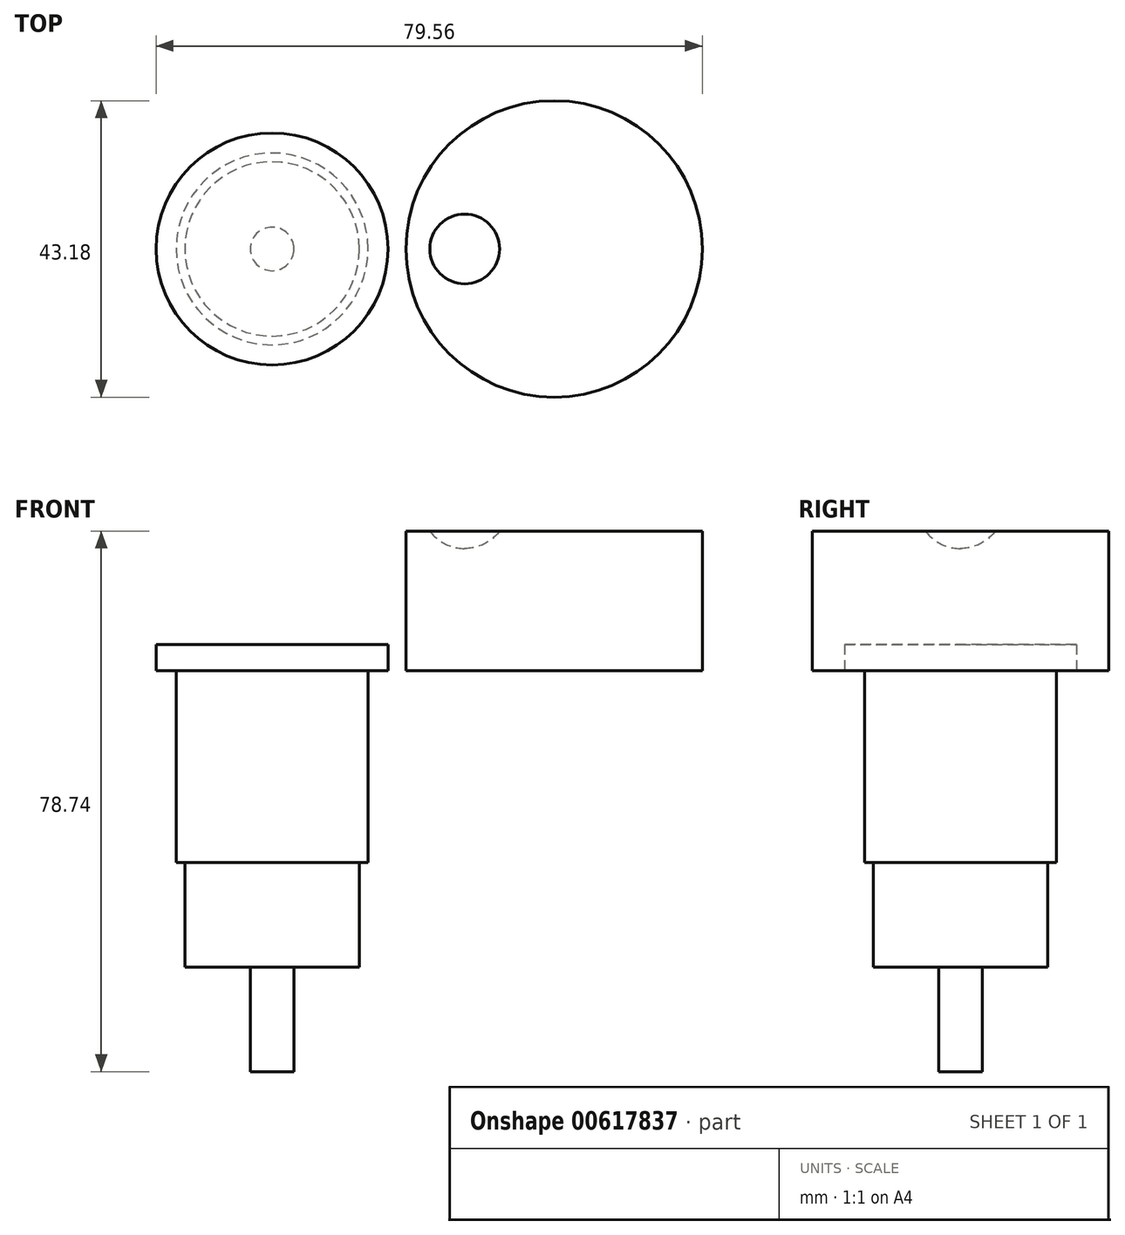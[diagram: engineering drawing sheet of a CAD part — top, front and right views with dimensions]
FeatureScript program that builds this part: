
annotation { "Feature Type Name" : "Feature", "Feature Type Description" : "" }
export const myFeature = defineFeature(function(context is Context, id is Id, definition is map)
    precondition{}
    {
        {
            var Q0;
            Q0=qCreatedBy(makeId("Top.planeOp"),FACE);
            var sketch = newSketch(context, id + "F0", { "sketchPlane" : qUnion([Q0])});
            skCircle(sketch, "E0", {"center": v(0, 0) * mm, "radius": 16.9 * mm});
            skCircle(sketch, "E1", {"center": v(0, 0) * mm, "radius": 13.97 * mm});
            skCircle(sketch, "E2", {"center": v(0, 0) * mm, "radius": 12.7 * mm});
            skCircle(sketch, "E3", {"center": v(0, 0) * mm, "radius": 3.18 * mm});
            skCircle(sketch, "E4", {"center": v(41.08, 0) * mm, "radius": 21.59 * mm});
            skSolve(sketch);
        }
        {
            var Q0;
            Q0=makeQuery(id+"F0.imprint","IMPRINT",FACE,{"disambiguationData":[TD([[makeQuery(id+"F0.imprint","IMPRINT",EDGE,{"derivedFrom":sQuery(id+"F0.wireOp",EDGE,"E3")}),1.0]])]});
            extrude(context, id + "F1", {"entities" : qUnion([Q0]), "oppositeDirection" : true, "depth" : 58.42 * mm, "offsetDistance" : 25.4 * mm});
        }
        {
            var Q0;
            Q0=makeQuery(id+"F0.imprint","IMPRINT",FACE,{"disambiguationData":[TD([[makeQuery(id+"F0.imprint","IMPRINT",EDGE,{"derivedFrom":sQuery(id+"F0.wireOp",EDGE,"E2")}),1.0]])]});
            extrude(context, id + "F2", {"entities" : qUnion([Q0]), "operationType" : NewBodyOperationType.ADD, "oppositeDirection" : true, "depth" : 43.18 * mm, "offsetDistance" : 25.4 * mm});
        }
        {
            var Q0;
            Q0=makeQuery(id+"F0.imprint","IMPRINT",FACE,{"disambiguationData":[TD([[makeQuery(id+"F0.imprint","IMPRINT",EDGE,{"derivedFrom":sQuery(id+"F0.wireOp",EDGE,"E1")}),1.0]])]});
            extrude(context, id + "F3", {"entities" : qUnion([Q0]), "operationType" : NewBodyOperationType.ADD, "oppositeDirection" : true, "depth" : 27.94 * mm, "offsetDistance" : 25.4 * mm});
        }
        {
            var Q0;
            Q0=makeQuery(id+"F0.imprint","IMPRINT",FACE,{"disambiguationData":[TD([[makeQuery(id+"F0.imprint","IMPRINT",EDGE,{"derivedFrom":sQuery(id+"F0.wireOp",EDGE,"E0")}),1.0]])]});
            var Q1;
            Q1=makeQuery(id+"F0.imprint","IMPRINT",FACE,{"disambiguationData":[TD([[makeQuery(id+"F0.imprint","IMPRINT",EDGE,{"derivedFrom":sQuery(id+"F0.wireOp",EDGE,"E1")}),1.0]])]});
            var Q2;
            Q2=makeQuery(id+"F0.imprint","IMPRINT",FACE,{"disambiguationData":[TD([[makeQuery(id+"F0.imprint","IMPRINT",EDGE,{"derivedFrom":sQuery(id+"F0.wireOp",EDGE,"E2")}),1.0]])]});
            var Q3;
            Q3=makeQuery(id+"F0.imprint","IMPRINT",FACE,{"disambiguationData":[TD([[makeQuery(id+"F0.imprint","IMPRINT",EDGE,{"derivedFrom":sQuery(id+"F0.wireOp",EDGE,"E3")}),1.0]])]});
            extrude(context, id + "F4", {"entities" : qUnion([Q0, Q1, Q2, Q3]), "operationType" : NewBodyOperationType.ADD, "depth" : 3.8 * mm, "offsetDistance" : 25.4 * mm});
        }
        {
            var Q0;
            Q0=makeQuery(id+"F0.imprint","IMPRINT",FACE,{"disambiguationData":[TD([[makeQuery(id+"F0.imprint","IMPRINT",EDGE,{"derivedFrom":sQuery(id+"F0.wireOp",EDGE,"E4")}),1.0]])]});
            extrude(context, id + "F5", {"entities" : qUnion([Q0]), "depth" : 20.32 * mm, "offsetDistance" : 25.4 * mm});
        }
        {
            var Q0;
            Q0=makeQuery(id+"F5.opExtrude","CAP_FACE",FACE,{"disambiguationData":[OSD([sQuery(id+"F0.wireOp",EDGE,"E4")])],"isStart":false});
            var sketch = newSketch(context, id + "F6", { "sketchPlane" : qUnion([Q0])});
            skCircle(sketch, "E5", {"center": v(28.06, 0) * mm, "radius": 5.08 * mm});
            skSolve(sketch);
        }
        {
            var Q0;
            Q0=makeQuery(id+"F6.imprint","IMPRINT",FACE,{"disambiguationData":[TD([[makeQuery(id+"F6.imprint","IMPRINT",EDGE,{"derivedFrom":sQuery(id+"F6.wireOp",EDGE,"E5")}),1.0]])]});
            extrude(context, id + "F7", {"entities" : qUnion([Q0]), "operationType" : NewBodyOperationType.REMOVE, "oppositeDirection" : true, "depth" : 2.54 * mm, "offsetDistance" : 25.4 * mm});
        }
        {
            var Q0;
            Q0=makeQuery(id+"F7.boolean.opBoolean","COPY",EDGE,{"derivedFrom":makeQuery(id+"F7.opExtrude","CAP_EDGE",EDGE,{"disambiguationData":[OSD([sQuery(id+"F6.wireOp",EDGE,"E5")])],"isStart":false})});
            fillet(context, id + "F8", {"entities" : qUnion([Q0]), "radius" : 6.22 * mm, "tangentPropagation" : true, "allowEdgeOverflow" : false});
        }
    });
